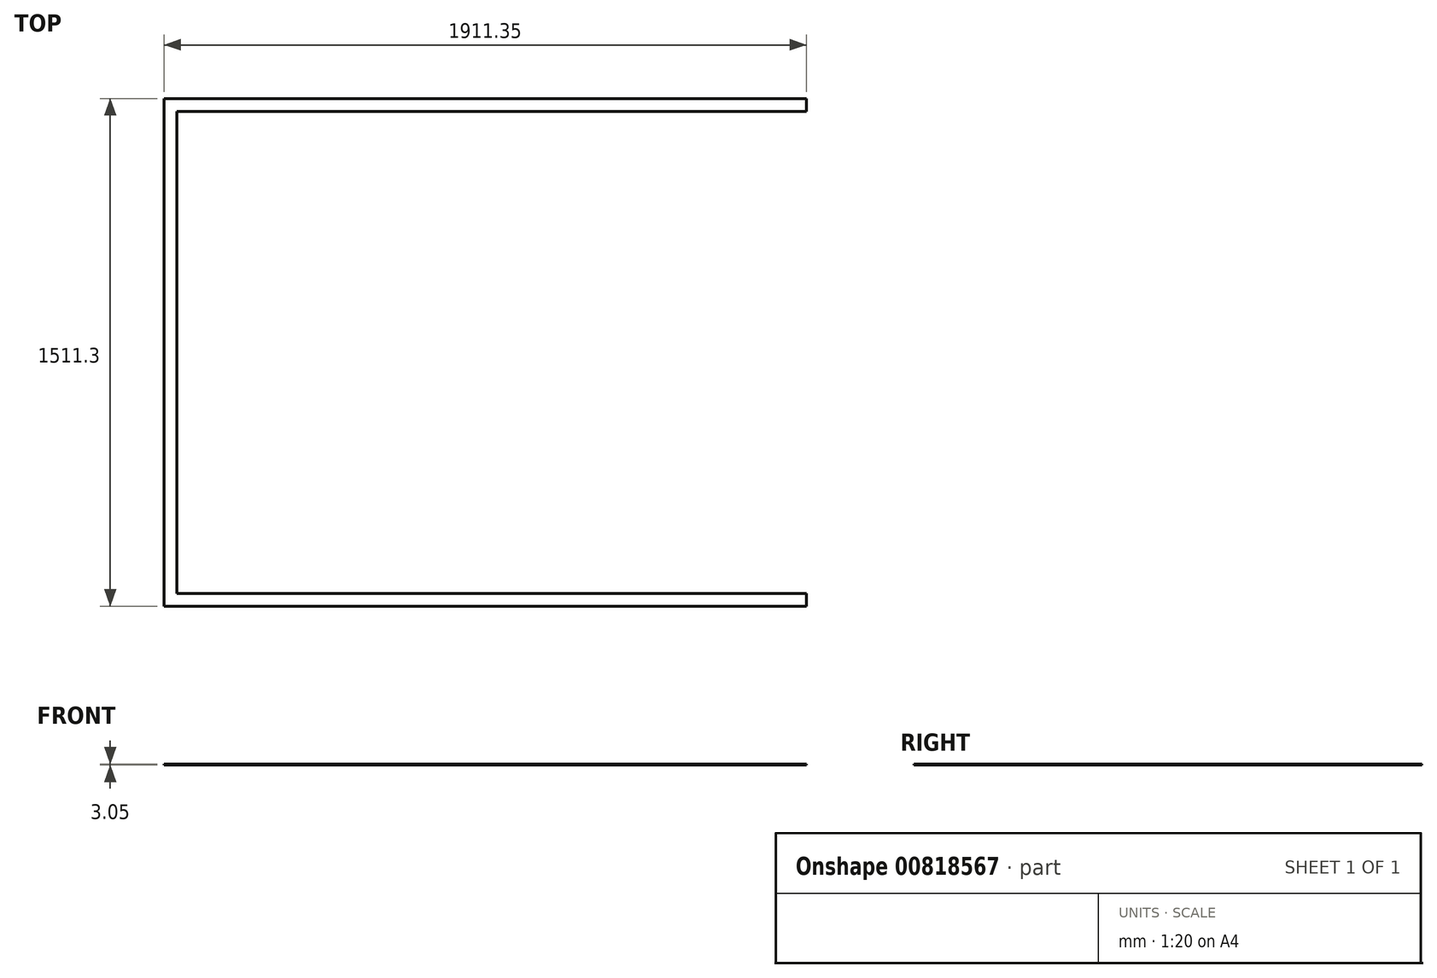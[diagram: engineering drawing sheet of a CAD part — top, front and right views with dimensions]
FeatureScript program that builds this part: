
annotation { "Feature Type Name" : "Feature", "Feature Type Description" : "" }
export const myFeature = defineFeature(function(context is Context, id is Id, definition is map)
    precondition{}
    {
        {
            var Q0;
            Q0=qCreatedBy(makeId("Top.planeOp"),FACE);
            var sketch = newSketch(context, id + "F0", { "sketchPlane" : qUnion([Q0])});
            skLineSegment(sketch, "E0.bottom", {"start": v(-956.89, 830.64) * mm, "end": v(954.46, 830.64) * mm});
            skLineSegment(sketch, "E0.top", {"start": v(-956.89, -680.66) * mm, "end": v(954.46, -680.66) * mm});
            skLineSegment(sketch, "E0.left", {"start": v(-956.89, 830.64) * mm, "end": v(-956.89, -680.66) * mm});
            skLineSegment(sketch, "E0.right", {"start": v(954.46, 830.64) * mm, "end": v(954.46, -680.66) * mm});
            skLineSegment(sketch, "E1.bottom", {"start": v(954.46, 792.54) * mm, "end": v(-918.79, 792.54) * mm});
            skLineSegment(sketch, "E1.top", {"start": v(954.46, -642.56) * mm, "end": v(-918.79, -642.56) * mm});
            skLineSegment(sketch, "E1.left", {"start": v(954.46, 792.54) * mm, "end": v(954.46, -642.56) * mm});
            skLineSegment(sketch, "E1.right", {"start": v(-918.79, 792.54) * mm, "end": v(-918.79, -642.56) * mm});
            skSolve(sketch);
        }
        {
            var Q0;
            {var subQ1=sQuery(id+"F0.wireOp",EDGE,"E0.bottom");Q0=makeQuery(id+"F0.imprint","IMPRINT",FACE,{"disambiguationData":[TD([[makeQuery(id+"F0.imprint","IMPRINT",EDGE,{"derivedFrom":subQ1}),-1.0]])]});}
            extrude(context, id + "F1", {"entities" : qUnion([Q0]), "depth" : 3.05 * mm, "offsetDistance" : 25.4 * mm});
        }
    });
